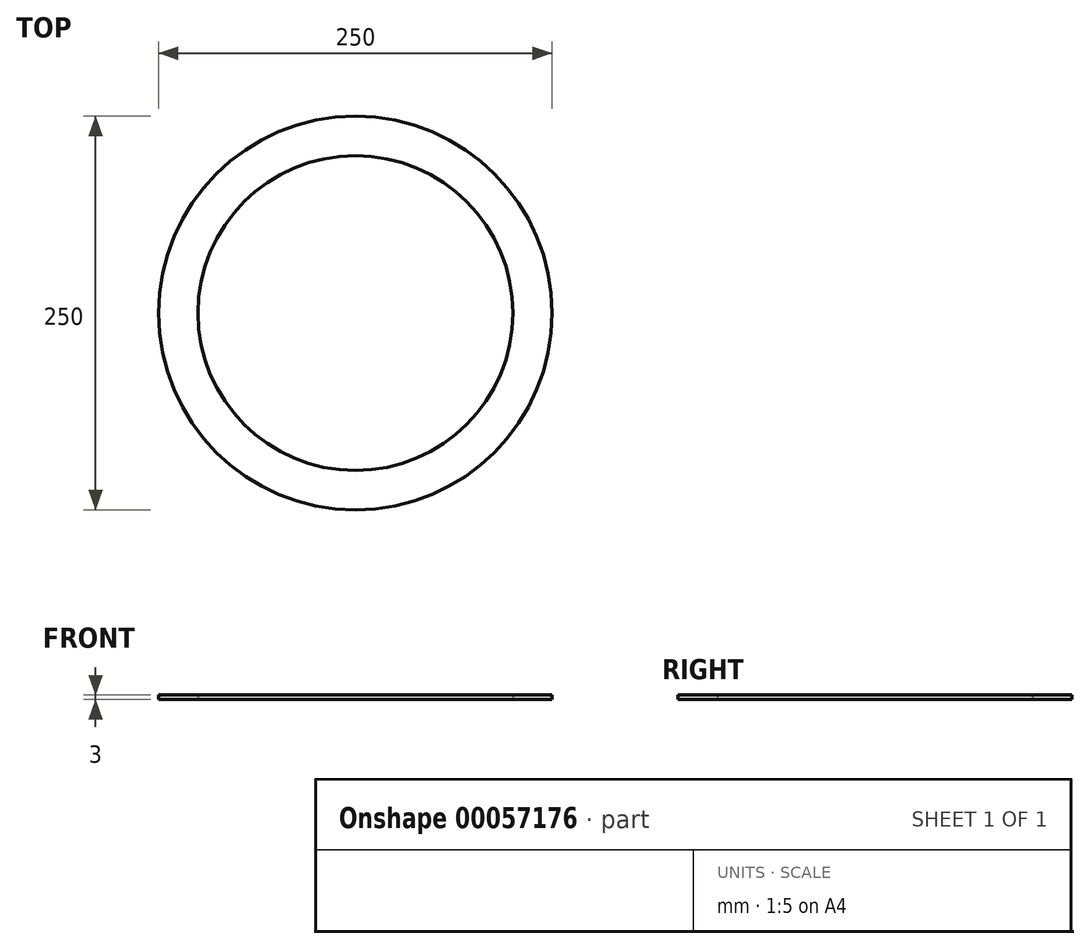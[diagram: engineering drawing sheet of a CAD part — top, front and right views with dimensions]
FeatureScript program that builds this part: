
annotation { "Feature Type Name" : "Feature", "Feature Type Description" : "" }
export const myFeature = defineFeature(function(context is Context, id is Id, definition is map)
    precondition{}
    {
        {
            var Q0;
            Q0=qCreatedBy(makeId("Top.planeOp"),FACE);
            var sketch = newSketch(context, id + "F0", { "sketchPlane" : qUnion([Q0])});
            skCircle(sketch, "E0", {"center": v(0, 0) * mm, "radius": 90 * mm});
            skCircle(sketch, "E1", {"center": v(0, 0) * mm, "radius": 100 * mm});
            skCircle(sketch, "E2", {"center": v(0, 0) * mm, "radius": 130 * mm});
            skCircle(sketch, "E3", {"center": v(0, 0) * mm, "radius": 125 * mm});
            skSolve(sketch);
        }
        {
            var Q0;
            Q0=makeQuery(id+"F0.imprint","IMPRINT",FACE,{"disambiguationData":[TD([[makeQuery(id+"F0.imprint","IMPRINT",EDGE,{"derivedFrom":sQuery(id+"F0.wireOp",EDGE,"E0")}),1.0]])]});
            var Q1;
            Q1=makeQuery(id+"F0.imprint","IMPRINT",FACE,{"disambiguationData":[TD([[makeQuery(id+"F0.imprint","IMPRINT",EDGE,{"derivedFrom":sQuery(id+"F0.wireOp",EDGE,"E0")}),-1.0]])]});
            var Q2;
            Q2=makeQuery(id+"F0.imprint","IMPRINT",FACE,{"disambiguationData":[TD([[makeQuery(id+"F0.imprint","IMPRINT",EDGE,{"derivedFrom":sQuery(id+"F0.wireOp",EDGE,"E1")}),-1.0]])]});
            extrude(context, id + "F1", {"entities" : qUnion([Q0, Q1, Q2]), "depth" : 3 * mm});
        }
        {
            var Q0;
            Q0=makeQuery(id+"F0.imprint","IMPRINT",FACE,{"disambiguationData":[TD([[makeQuery(id+"F0.imprint","IMPRINT",EDGE,{"derivedFrom":sQuery(id+"F0.wireOp",EDGE,"E0")}),1.0]])]});
            var Q1;
            Q1=makeQuery(id+"F0.imprint","IMPRINT",FACE,{"disambiguationData":[TD([[makeQuery(id+"F0.imprint","IMPRINT",EDGE,{"derivedFrom":sQuery(id+"F0.wireOp",EDGE,"E0")}),-1.0]])]});
            extrude(context, id + "F2", {"entities" : qUnion([Q0, Q1]), "depth" : 3 * mm});
        }
    });
